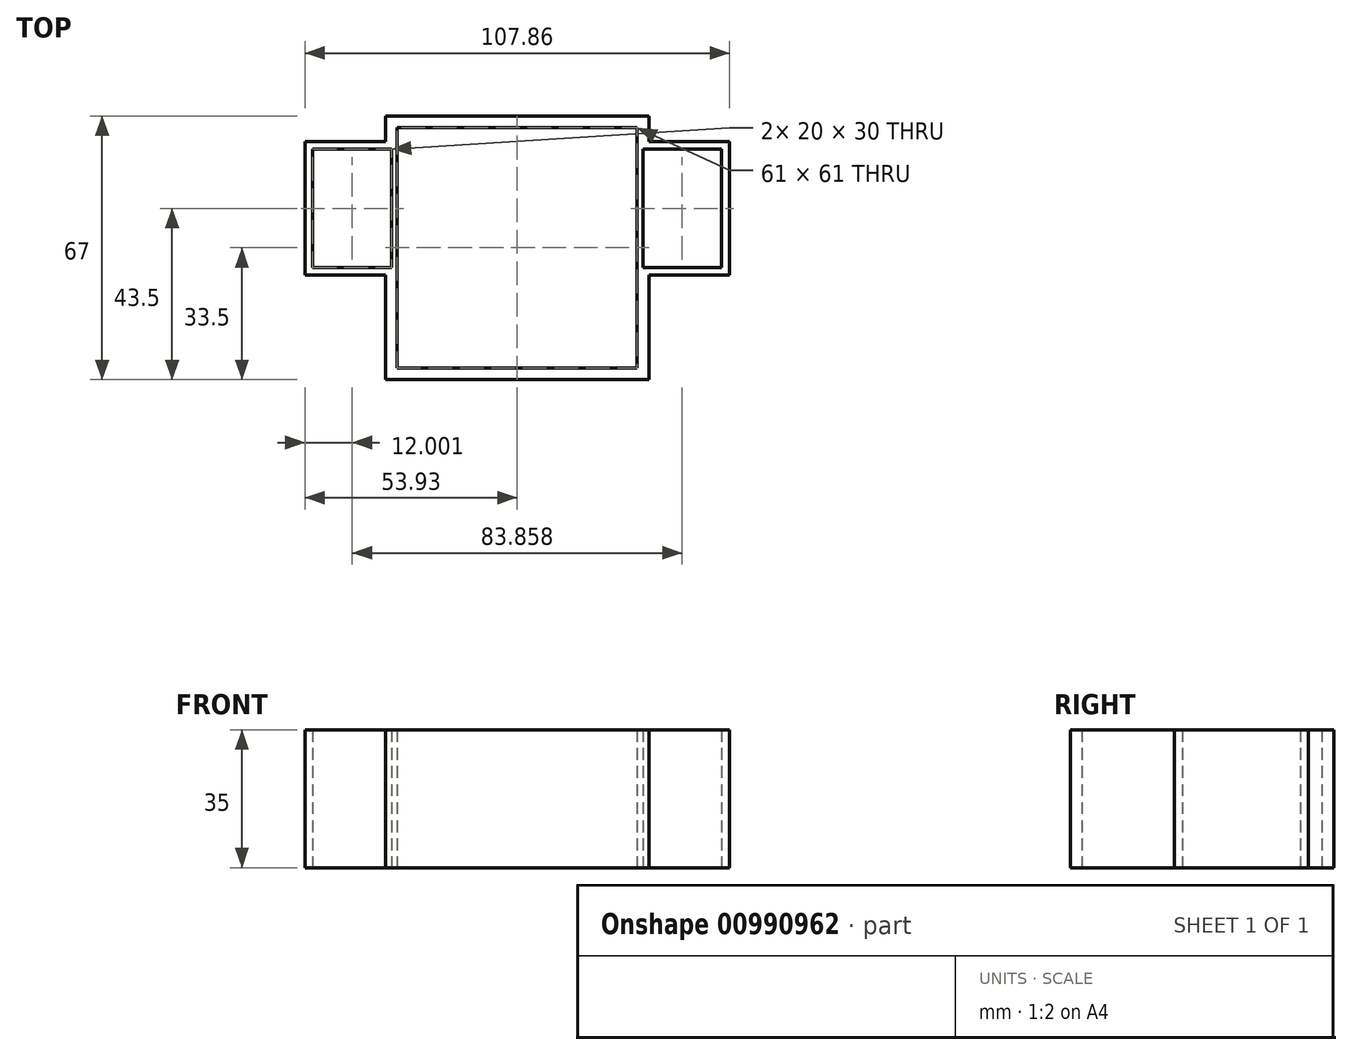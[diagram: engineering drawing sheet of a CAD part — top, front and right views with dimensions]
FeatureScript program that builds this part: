
annotation { "Feature Type Name" : "Feature", "Feature Type Description" : "" }
export const myFeature = defineFeature(function(context is Context, id is Id, definition is map)
    precondition{}
    {
        {
            var Q0;
            Q0=qCreatedBy(makeId("Top.planeOp"),FACE);
            var sketch = newSketch(context, id + "F0", { "sketchPlane" : qUnion([Q0])});
            skLineSegment(sketch, "E0.bottom", {"start": v(30.5, -30.5) * mm, "end": v(-30.5, -30.5) * mm});
            skLineSegment(sketch, "E0.top", {"start": v(30.5, 30.5) * mm, "end": v(-30.5, 30.5) * mm});
            skLineSegment(sketch, "E0.left", {"start": v(30.5, -30.5) * mm, "end": v(30.5, 30.5) * mm});
            skLineSegment(sketch, "E0.right", {"start": v(-30.5, -30.5) * mm, "end": v(-30.5, 30.5) * mm});
            skPoint(sketch, "E0.middle", {"position": v(0, 0) * mm});
            skLineSegment(sketch, "E1", {"start": v(-71.26, 0) * mm, "end": v(73.47, 0) * mm, "construction": true});
            skLineSegment(sketch, "E2", {"start": v(0, 53.8) * mm, "end": v(0, -68.32) * mm, "construction": true});
            skLineSegment(sketch, "E3.bottom", {"start": v(-31.93, 25) * mm, "end": v(-51.93, 25) * mm});
            skLineSegment(sketch, "E3.top", {"start": v(-31.93, -5) * mm, "end": v(-51.93, -5) * mm});
            skLineSegment(sketch, "E3.left", {"start": v(-31.93, 25) * mm, "end": v(-31.93, -5) * mm});
            skLineSegment(sketch, "E3.right", {"start": v(-51.93, 25) * mm, "end": v(-51.93, -5) * mm});
            skPoint(sketch, "E4", {"position": v(-51.93, 0) * mm});
            skPoint(sketch, "E5", {"position": v(-30.5, 25) * mm});
            skLineSegment(sketch, "E6.0", {"start": v(-30.5, -7) * mm, "end": v(-53.93, -7) * mm});
            skLineSegment(sketch, "E6.1", {"start": v(-53.93, 27) * mm, "end": v(-53.93, -7) * mm});
            skLineSegment(sketch, "E6.2", {"start": v(-30.5, 27) * mm, "end": v(-53.93, 27) * mm});
            skLineSegment(sketch, "E7.MirrorCS", {"start": v(30.5, 27) * mm, "end": v(53.93, 27) * mm});
            skLineSegment(sketch, "E8.MirrorCS", {"start": v(31.93, 25) * mm, "end": v(51.93, 25) * mm});
            skLineSegment(sketch, "E9.MirrorCS", {"start": v(31.93, -5) * mm, "end": v(51.93, -5) * mm});
            skLineSegment(sketch, "E10.MirrorCS", {"start": v(30.5, -7) * mm, "end": v(53.93, -7) * mm});
            skLineSegment(sketch, "E11.MirrorCS", {"start": v(31.93, 25) * mm, "end": v(31.93, -5) * mm});
            skLineSegment(sketch, "E12.MirrorCS", {"start": v(51.93, 25) * mm, "end": v(51.93, -5) * mm});
            skLineSegment(sketch, "E13.MirrorCS", {"start": v(53.93, 27) * mm, "end": v(53.93, -7) * mm});
            skLineSegment(sketch, "E14", {"start": v(-33.5, 27) * mm, "end": v(-33.5, 33.5) * mm});
            skLineSegment(sketch, "E15", {"start": v(-33.5, 33.5) * mm, "end": v(33.5, 33.5) * mm});
            skLineSegment(sketch, "E16", {"start": v(33.5, 33.5) * mm, "end": v(33.5, 27) * mm});
            skLineSegment(sketch, "E17", {"start": v(-33.5, -7) * mm, "end": v(-33.5, -33.5) * mm});
            skLineSegment(sketch, "E18", {"start": v(-33.5, -33.5) * mm, "end": v(33.5, -33.5) * mm});
            skLineSegment(sketch, "E19", {"start": v(33.5, -33.5) * mm, "end": v(33.5, -7) * mm});
            skSolve(sketch);
        }
        {
            var Q0;
            Q0=makeQuery(id+"F0.imprint","IMPRINT",FACE,{"disambiguationData":[TD([[makeQuery(id+"F0.imprint","IMPRINT",EDGE,{"derivedFrom":sQuery(id+"F0.wireOp",EDGE,"E3.bottom")}),-1.0]])]});
            var Q1;
            {var subQ5=sQuery(id+"F0.wireOp",EDGE,"E0.top");Q1=makeQuery(id+"F0.imprint","IMPRINT",FACE,{"disambiguationData":[TD([[makeQuery(id+"F0.imprint","IMPRINT",EDGE,{"derivedFrom":subQ5}),-1.0]])]});}
            var Q2;
            Q2=makeQuery(id+"F0.imprint","IMPRINT",FACE,{"disambiguationData":[TD([[makeQuery(id+"F0.imprint","IMPRINT",EDGE,{"derivedFrom":sQuery(id+"F0.wireOp",EDGE,"E8.MirrorCS")}),1.0]])]});
            var Q3;
            {var subQ5=sQuery(id+"F0.wireOp",EDGE,"E0.bottom");Q3=makeQuery(id+"F0.imprint","IMPRINT",FACE,{"disambiguationData":[TD([[makeQuery(id+"F0.imprint","IMPRINT",EDGE,{"derivedFrom":subQ5}),1.0]])]});}
            extrude(context, id + "F1", {"entities" : qUnion([Q0, Q1, Q2, Q3]), "depth" : 35 * mm, "offsetDistance" : 25 * mm});
        }
    });
